# Revit family: spectral_stora_stora-qp-led_5200_840_mps_1bbb
name_source: partatom
category: Lighting Fixtures
revit_build: Autodesk Revit 2016 (Build: 20150220_1215(x64)
units: mm (PartAtom-declared; Revit-internal decimal feet)

## family parameters
Cut with Voids When Loaded = No
Host = Face
Light Source = No
Part Type = Normal
Room Calculation Point = No
Round Connector Dimension = Use Diameter
Shared = No

## types (1)
- SPECTRAL STORA (1 x )
    Apparent Load = 0 VA
    Approval mark = CE
    CIE Flux Codes = 64 90 97 96 73
    Control Gear = Electronic transformer
    Default Elevation = 1800 mm
    Description = SPC0620002
STORA pendant LED luminaire

Design:
Square luminaire element with microprism panel mounted in a profile frame made of power-coated aluminium. The luminaire is suspended by a wire
pendant with ceiling fixture and transparent connecting cable with rectangular powder-coated ceiling junction box. The cable length can be adjusted at the ceiling junction box, the steel wire can be steplessly height adjusted at the luminaire. At the top of the luminaire, the control gear is accommodated under a cover which can be removed for maintenance using key-shaped holes. The LED module is formed as a square flat board. Luminaire with heat-resistant wiring. Variant suitable for office workplaces with microprism panel MPS. The LED spots are visible as circles on the microprism panel. Light colours 4000 K (840) or 3000 K (830). Also in a dimmable version. Protection rating IP20, Protection class I.

Colour:
Frame – similar to RAL 9016 white silk matt
    Height = 50 mm
    Lamp = 1 x
    Lamp count = 1
    Length = 580 mm
    Luminous efficacy = 0 lm/W
    Manufacturer = Ridi
    ModVariant = No
    Model = STORA-QP-LED 5200/840 MPS
    Mounting Place = Ceiling
    Mounting Type = Pendant
    Number of Poles = 1
    OnlyDefault = Yes
    Power Factor = 1
    Product Name = SPECTRAL STORA
    Product group = Pendant luminaire
    ProductGroupID = 9
    Protection Class = Protection class
    Protection Degree = IP 20
    RlxData = <blob elided: 14265 chars, md5=31e25b6d>
    Socket = socket
    Standby Power = 0 W
    System Light Flux = 0 lm
    System Power = 0 W
    Type Image = stora-qp_512.jpg
    URL = http://reluxnet.relux.com
    VarID = 1
    Voltage = 0 V
    Weight = 0.00 kg
    Width = 580 mm

## geometry (parser evidence)
native form markers: Blend x4, Sweep x13
no freeform markers — native parametric forms only
